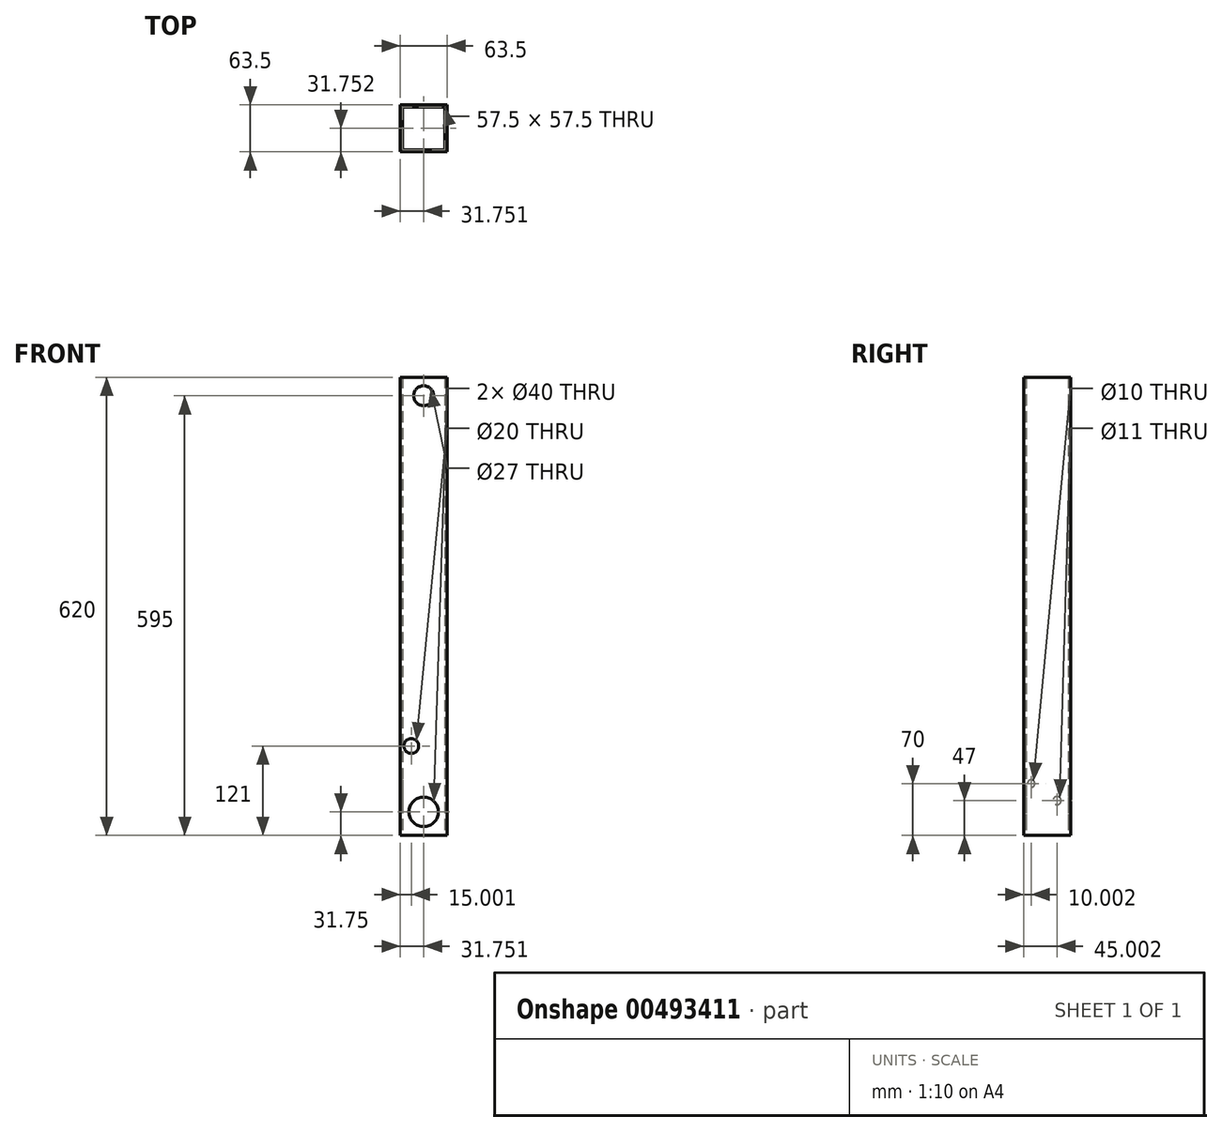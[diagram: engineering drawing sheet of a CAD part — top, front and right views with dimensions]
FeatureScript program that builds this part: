
annotation { "Feature Type Name" : "Feature", "Feature Type Description" : "" }
export const myFeature = defineFeature(function(context is Context, id is Id, definition is map)
    precondition{}
    {
        {
            var Q0;
            Q0=qCreatedBy(makeId("Top.planeOp"),FACE);
            var sketch = newSketch(context, id + "F0", { "sketchPlane" : qUnion([Q0])});
            skLineSegment(sketch, "E0.bottom", {"start": v(-22.05, 15.04) * mm, "end": v(35.45, 15.04) * mm});
            skLineSegment(sketch, "E0.top", {"start": v(-22.05, -42.46) * mm, "end": v(35.45, -42.46) * mm});
            skLineSegment(sketch, "E0.left", {"start": v(-22.05, 15.04) * mm, "end": v(-22.05, -42.46) * mm});
            skLineSegment(sketch, "E0.right", {"start": v(35.45, 15.04) * mm, "end": v(35.45, -42.46) * mm});
            skLineSegment(sketch, "E1.bottom", {"start": v(-25.05, 18.04) * mm, "end": v(38.45, 18.04) * mm});
            skLineSegment(sketch, "E1.top", {"start": v(-25.05, -45.46) * mm, "end": v(38.45, -45.46) * mm});
            skLineSegment(sketch, "E1.left", {"start": v(-25.05, 18.04) * mm, "end": v(-25.05, -45.46) * mm});
            skLineSegment(sketch, "E1.right", {"start": v(38.45, 18.04) * mm, "end": v(38.45, -45.46) * mm});
            skSolve(sketch);
        }
        {
            var Q0;
            Q0 = qSketchRegion(id + "F0", true);
            extrude(context, id + "F1", {"entities" : qUnion([Q0]), "flatOperationType" : FlatOperationType.REMOVE, "offsetDistance" : 25 * mm, "depth" : 620 * mm, "domain" : OperationDomain.MODEL});
        }
        {
            var Q0;
            Q0=makeQuery(id+"F1.opExtrude","SWEPT_FACE",FACE,{"disambiguationData":[OSD([sQuery(id+"F0.wireOp",EDGE,"E1.top")])]});
            var sketch = newSketch(context, id + "F2", { "sketchPlane" : qUnion([Q0])});
            skCircle(sketch, "E2", {"center": v(-10.05, 121) * mm, "radius": 10 * mm});
            skSolve(sketch);
        }
        {
            var Q0;
            Q0 = qSketchRegion(id + "F2", true);
            extrude(context, id + "F3", {"entities" : qUnion([Q0]), "operationType" : NewBodyOperationType.REMOVE, "oppositeDirection" : true, "depth" : 3 * mm, "offsetDistance" : 25 * mm});
        }
        {
            var Q0;
            Q0=makeQuery(id+"F1.opExtrude","SWEPT_FACE",FACE,{"disambiguationData":[OSD([sQuery(id+"F0.wireOp",EDGE,"E1.bottom")])]});
            var sketch = newSketch(context, id + "F4", { "sketchPlane" : qUnion([Q0])});
            skCircle(sketch, "E3", {"center": v(-6.7, 31.75) * mm, "radius": 20 * mm});
            skSolve(sketch);
        }
        {
            var Q0;
            Q0 = qSketchRegion(id + "F4", true);
            extrude(context, id + "F5", {"entities" : qUnion([Q0]), "operationType" : NewBodyOperationType.REMOVE, "flatOperationType" : FlatOperationType.REMOVE, "oppositeDirection" : true, "depth" : 70 * mm, "offsetDistance" : 25 * mm, "domain" : OperationDomain.MODEL});
        }
        {
            var Q0;
            Q0=makeQuery(id+"F1.opExtrude","SWEPT_FACE",FACE,{"disambiguationData":[OSD([sQuery(id+"F0.wireOp",EDGE,"E1.top")])]});
            var sketch = newSketch(context, id + "F6", { "sketchPlane" : qUnion([Q0])});
            skCircle(sketch, "E4", {"center": v(6.7, 595) * mm, "radius": 13.5 * mm});
            skSolve(sketch);
        }
        {
            var Q0;
            Q0 = qSketchRegion(id + "F6", true);
            extrude(context, id + "F7", {"entities" : qUnion([Q0]), "operationType" : NewBodyOperationType.REMOVE, "oppositeDirection" : true, "depth" : 3 * mm, "offsetDistance" : 25 * mm});
        }
        {
            var Q0;
            Q0=makeQuery(id+"F1.opExtrude","SWEPT_FACE",FACE,{"disambiguationData":[OSD([sQuery(id+"F0.wireOp",EDGE,"E1.left")])]});
            var sketch = newSketch(context, id + "F8", { "sketchPlane" : qUnion([Q0])});
            skCircle(sketch, "E5", {"center": v(0.46, 47) * mm, "radius": 5.5 * mm});
            skCircle(sketch, "E6", {"center": v(35.46, 70) * mm, "radius": 5 * mm});
            skSolve(sketch);
        }
        {
            var Q0;
            Q0 = qSketchRegion(id + "F8", true);
            extrude(context, id + "F9", {"entities" : qUnion([Q0]), "operationType" : NewBodyOperationType.REMOVE, "oppositeDirection" : true, "depth" : 3 * mm, "offsetDistance" : 25 * mm});
        }
    });
